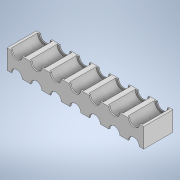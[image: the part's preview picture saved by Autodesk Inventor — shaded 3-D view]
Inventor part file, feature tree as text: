
AUTODESK INVENTOR PART (.ipt)
format: ipt  version: 2021 (Build 250183000, 183)  size: 257,024 bytes
history: native  units: mm
features: extrude x4, sketch x4, pattern_linear x1
ambient origin geometry x8: Origin, YZ Plane, XZ Plane, XY Plane, X Axis, Y Axis, Z Axis, Center Point
bodies: Solid1 (feature_tree)
feature tree (9):
  extrude  "Extrusion1"  Depth=1.0mm
  pattern_linear  "Rectangular Pattern1"  Spacing1=8.0mm  [1 undecoded]
  extrude  "Extrusion2"  Depth=8.0mm
  extrude  "Extrusion3"  Depth=8.0mm
  extrude  "Extrusion4"  Depth=11.0mm TaperAngle=0.0deg
  sketch  "Sketch1"  dims[d0=6.0mm d1=1.0mm]
  sketch  "Sketch2"  dims[d2=1.0mm]
  sketch  "Sketch3"  dims[d3=8.0mm]
  sketch  "Sketch4"  dims[d4=6.0mm d5=8.0mm d6=8.0mm d7=8.0mm d8=11.0mm d9=0.0mm d10=70.0mm d12=8.0mm d13=0.5mm d14=0.0mm d15=0.5mm d16=0.0mm d17=4.5mm d18=4.5mm d19=4.0mm d20=4.0mm d21=70.0mm d23=8.0mm d24=10.0mm d26=10.0mm d28=50.0mm d29=0.0mm d30=20.0mm d31=0.0mm]
note: 1 required parameter value undecoded (feature->parameter linkage not recoverable at this tier; creation-order binding heuristic only, values carry confidence <= 0.55)
